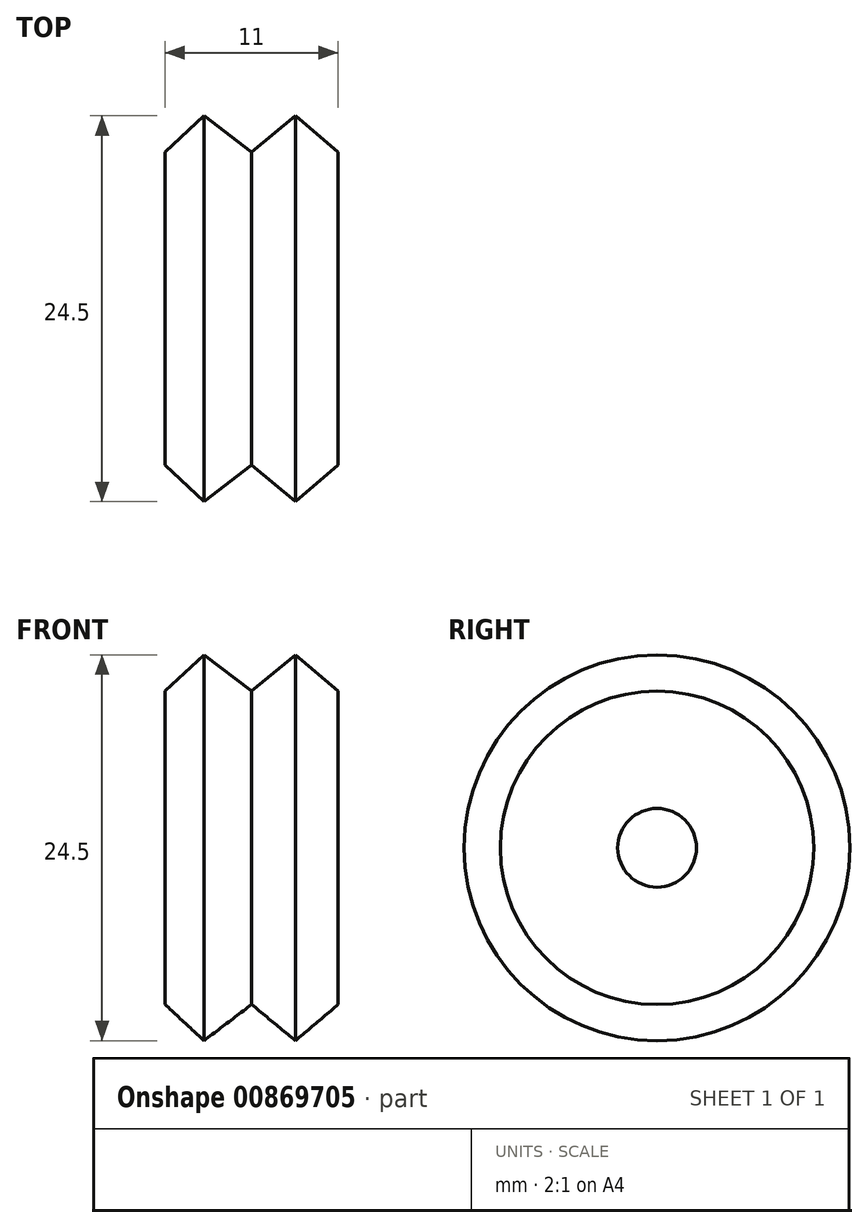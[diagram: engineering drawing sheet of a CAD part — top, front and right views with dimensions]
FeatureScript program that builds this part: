
annotation { "Feature Type Name" : "Feature", "Feature Type Description" : "" }
export const myFeature = defineFeature(function(context is Context, id is Id, definition is map)
    precondition{}
    {
        {
            var Q0;
            Q0=qCreatedBy(makeId("Front.planeOp"),FACE);
            var sketch = newSketch(context, id + "F0", { "sketchPlane" : qUnion([Q0])});
            skLineSegment(sketch, "E0", {"start": v(-5.5, 2.5) * mm, "end": v(-5.5, 9.95) * mm});
            skLineSegment(sketch, "E1", {"start": v(-5.5, 9.95) * mm, "end": v(-3.03, 12.25) * mm});
            skLineSegment(sketch, "E2", {"start": v(-3.03, 12.25) * mm, "end": v(0, 9.95) * mm});
            skLineSegment(sketch, "E3", {"start": v(0, 9.95) * mm, "end": v(2.78, 12.25) * mm});
            skLineSegment(sketch, "E4", {"start": v(2.78, 12.25) * mm, "end": v(5.5, 9.95) * mm});
            skLineSegment(sketch, "E5", {"start": v(5.5, 9.95) * mm, "end": v(5.5, 2.5) * mm});
            skLineSegment(sketch, "E6", {"start": v(-28.65, 0) * mm, "end": v(21.9, 0) * mm});
            skLineSegment(sketch, "E7", {"start": v(5.5, 2.5) * mm, "end": v(-5.5, 2.5) * mm});
            skPoint(sketch, "E8.end.orphan", {"position": v(-5.5, 0) * mm});
            skPoint(sketch, "E8.start.orphan", {"position": v(5.5, 0) * mm});
            skSolve(sketch);
        }
        {
            var Q0;
            Q0=sQuery(id+"F0.wireOp",EDGE,"E1");
            var Q1;
            Q1=sQuery(id+"F0.wireOp",EDGE,"E2");
            var Q2;
            Q2=sQuery(id+"F0.wireOp",EDGE,"E3");
            var Q3;
            Q3=sQuery(id+"F0.wireOp",EDGE,"E4");
            var Q4;
            Q4=sQuery(id+"F0.wireOp",EDGE,"E5");
            var Q5;
            Q5=sQuery(id+"F0.wireOp",EDGE,"E0");
            var Q6;
            Q6=sQuery(id+"F0.wireOp",EDGE,"E6");
            revolve(context, id + "F1", {"bodyType" : ToolBodyType.SURFACE, "surfaceOperationType" : NewSurfaceOperationType.NEW, "surfaceEntities" : qUnion([Q0, Q1, Q2, Q3, Q4, Q5]), "axis" : qUnion([Q6]), "revolveType" : RevolveType.FULL});
        }
    });
